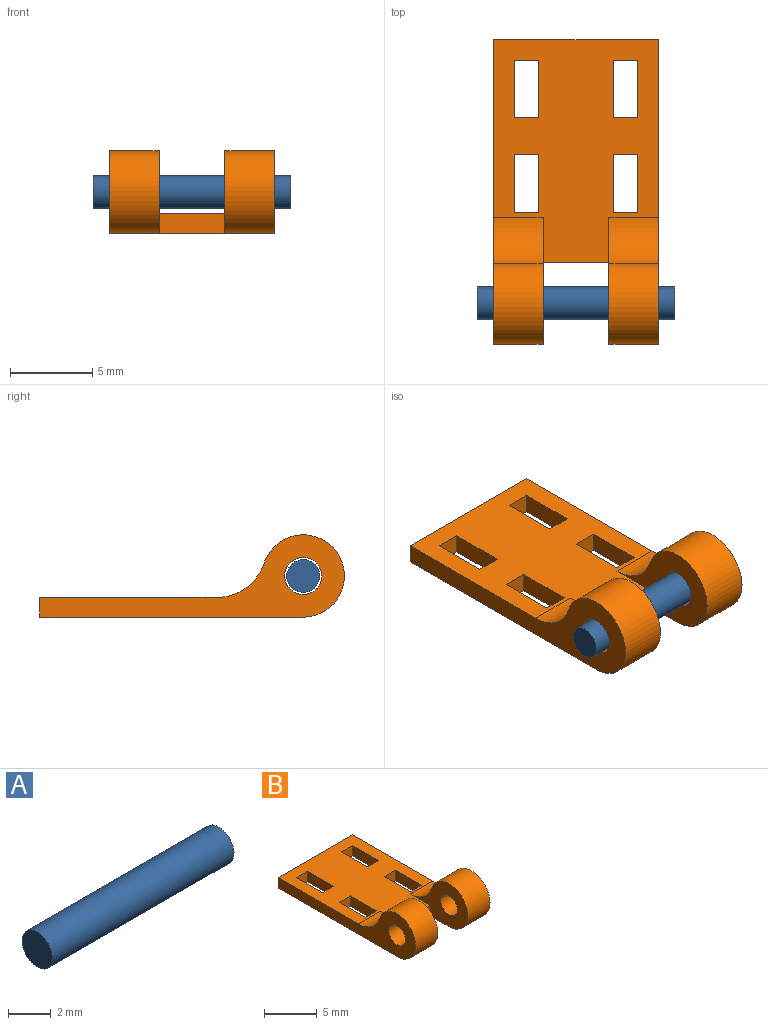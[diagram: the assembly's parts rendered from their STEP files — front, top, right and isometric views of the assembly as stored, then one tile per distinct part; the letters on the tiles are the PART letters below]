
ASSEMBLY  parts=2 mates=1
PART A: 3 faces, bbox 12x2x2 mm
  f0: cylinder r=1mm len=12mm, axis (-1,0,0), area 75.4mm2, adj f1,f2
  f1: plane 2x2mm, normal (1,0,0), area 3.1mm2, adj f0
  f2: plane 2x2mm, normal (-1,0,0), area 3.1mm2, adj f0
PART B: 30 faces, bbox 10x18.5x5 mm
  f0: plane 4x1.2mm, normal (0,-1,0), area 4.8mm2, adj f2,f3,f11,f12
  f1: cylinder r=3mm len=3mm, axis (-1,0,0), area 11.3mm2, adj f3,f4,f9,f12
  f2: plane 16x10mm, normal (0,0,-1), area 129mm2, adj f0,f4,f6,f7,f9,f10,f11,f12
  f3: plane 13.5x10mm, normal (0,0,1), area 97.6mm2, adj f0,f1,f6,f9,f10,f11,f12,f13
  f4: cylinder r=2.5mm len=5mm, axis (-1,0,0), area 33mm2, adj f1,f2,f9,f12
  f5: cylinder r=1.12mm len=3mm, axis (-1,0,0), area 21.2mm2, adj f9,f12
  f6: plane 10x1.2mm, normal (0,1,0), area 12mm2, adj f2,f3,f9,f10
  f7: cylinder r=2.5mm len=5mm, axis (-1,0,0), area 33mm2, adj f2,f10,f11,f29
  f8: cylinder r=1.12mm len=3mm, axis (-1,0,0), area 21.2mm2, adj f10,f11
  f9: plane 18.5x5mm, normal (1,0,0), area 34.6mm2, adj f1,f2,f3,f4,f5,f6
  f10: plane 18.5x5mm, normal (-1,0,0), area 34.6mm2, adj f2,f3,f6,f7,f8,f29
  f11: plane 7.73x5mm, normal (1,0,0), area 18.4mm2, adj f0,f2,f3,f7,f8,f29
  f12: plane 7.73x5mm, normal (-1,0,0), area 18.4mm2, adj f0,f1,f2,f3,f4,f5
  f13: plane 3.5x1.2mm, normal (1,0,0), area 4.2mm2, adj f2,f3,f14,f16
  f14: plane 1.5x1.2mm, normal (0,-1,0), area 1.8mm2, adj f2,f3,f13,f15
  f15: plane 3.5x1.2mm, normal (-1,0,0), area 4.2mm2, adj f2,f3,f14,f16
  f16: plane 1.5x1.2mm, normal (0,1,0), area 1.8mm2, adj f2,f3,f13,f15
  f17: plane 3.5x1.2mm, normal (-1,0,0), area 4.2mm2, adj f2,f3,f18,f20
  f18: plane 1.5x1.2mm, normal (0,1,0), area 1.8mm2, adj f2,f3,f17,f19
  f19: plane 3.5x1.2mm, normal (1,0,0), area 4.2mm2, adj f2,f3,f18,f20
  f20: plane 1.5x1.2mm, normal (0,-1,0), area 1.8mm2, adj f2,f3,f17,f19
  f21: plane 3.5x1.2mm, normal (-1,0,0), area 4.2mm2, adj f2,f3,f22,f24
  f22: plane 1.5x1.2mm, normal (0,1,0), area 1.8mm2, adj f2,f3,f21,f23
  f23: plane 3.5x1.2mm, normal (1,0,0), area 4.2mm2, adj f2,f3,f22,f24
  f24: plane 1.5x1.2mm, normal (0,-1,0), area 1.8mm2, adj f2,f3,f21,f23
  f25: plane 1.5x1.2mm, normal (0,-1,0), area 1.8mm2, adj f2,f3,f26,f28
  f26: plane 3.5x1.2mm, normal (-1,0,0), area 4.2mm2, adj f2,f3,f25,f27
  f27: plane 1.5x1.2mm, normal (0,1,0), area 1.8mm2, adj f2,f3,f26,f28
  f28: plane 3.5x1.2mm, normal (1,0,0), area 4.2mm2, adj f2,f3,f25,f27
  f29: cylinder r=3mm len=3mm, axis (-1,0,0), area 11.3mm2, adj f3,f7,f10,f11
PLACE A t=(-4.07,-13.63,-10.45)mm fixed
PLACE B rot(axis=(1,0,0),0deg) t=(-3.07,-5.63,-11.75)mm
MATE revolute A.f0 <-> B.f4  axis (-1,0,0) through (-4.07,-13.63,-10.45)mm
